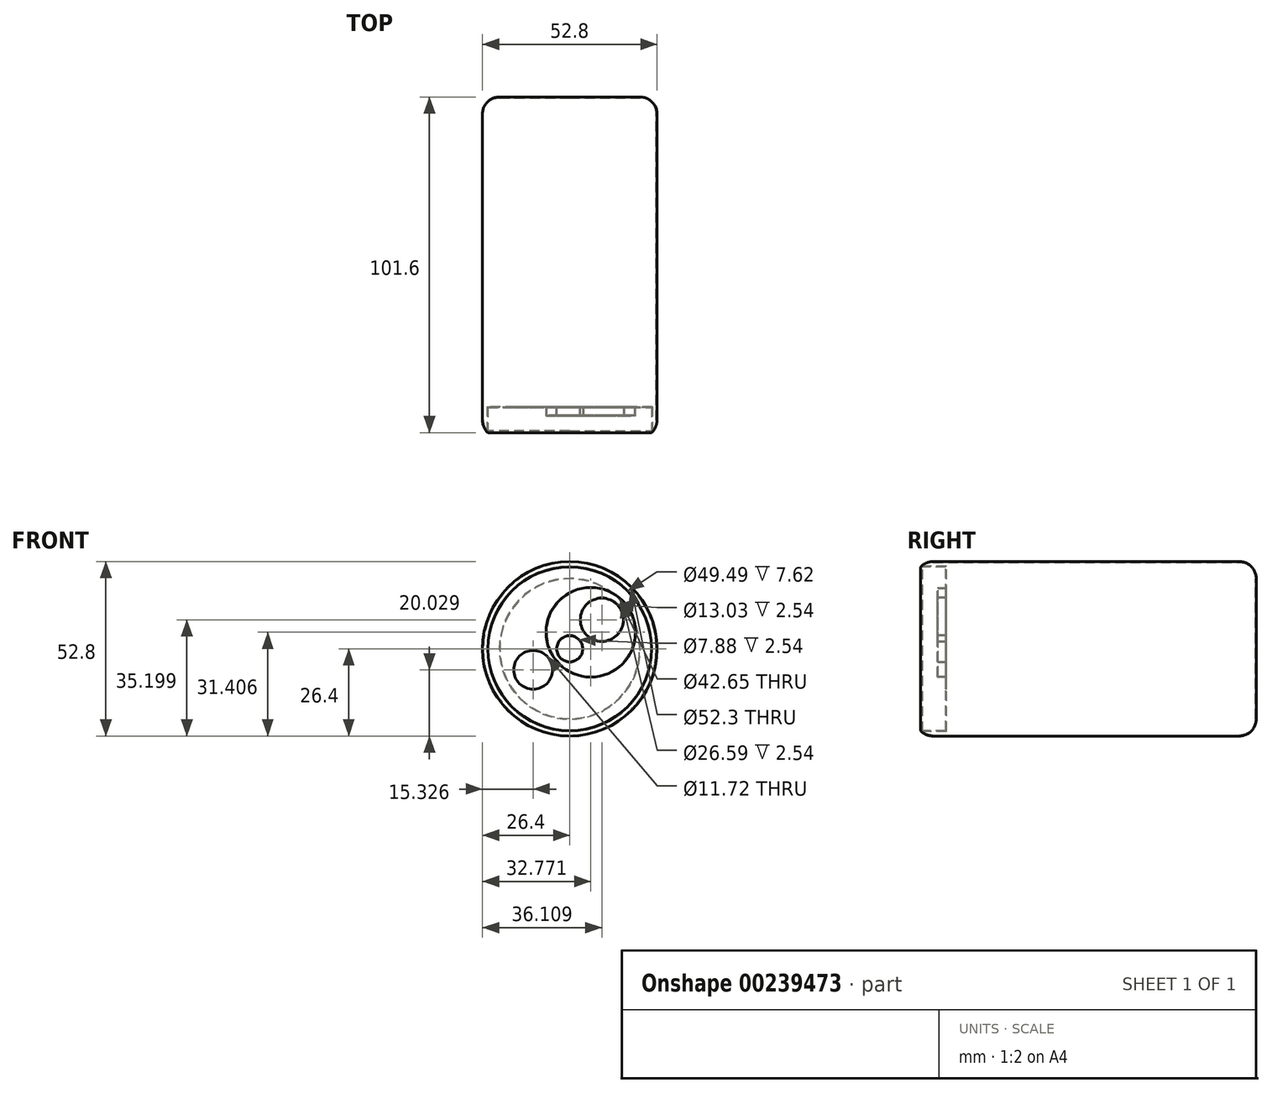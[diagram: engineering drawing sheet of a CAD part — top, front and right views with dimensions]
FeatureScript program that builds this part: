
annotation { "Feature Type Name" : "Feature", "Feature Type Description" : "" }
export const myFeature = defineFeature(function(context is Context, id is Id, definition is map)
    precondition{}
    {
        {
            var Q0;
            Q0=qCreatedBy(makeId("Front.planeOp"),FACE);
            var sketch = newSketch(context, id + "F0", { "sketchPlane" : qUnion([Q0])});
            skCircle(sketch, "E0", {"center": v(0, 0) * mm, "radius": 26.4 * mm});
            skSolve(sketch);
        }
        {
            var Q0;
            Q0=makeQuery(id+"F0.imprint","IMPRINT",FACE,{"disambiguationData":[TD([[makeQuery(id+"F0.imprint","IMPRINT",EDGE,{"derivedFrom":sQuery(id+"F0.wireOp",EDGE,"E0")}),1.0]])]});
            extrude(context, id + "F1", {"entities" : qUnion([Q0]), "depth" : 101.6 * mm});
        }
        {
            var Q0;
            Q0=makeQuery(id+"F1.opExtrude","CAP_FACE",FACE,{"disambiguationData":[OSD([sQuery(id+"F0.wireOp",EDGE,"E0")])],"isStart":false});
            var sketch = newSketch(context, id + "F2", { "sketchPlane" : qUnion([Q0])});
            skCircle(sketch, "E1", {"center": v(0, 0) * mm, "radius": 24.74 * mm});
            skSolve(sketch);
        }
        {
            var Q0;
            Q0=makeQuery(id+"F2.imprint","IMPRINT",FACE,{"disambiguationData":[TD([[makeQuery(id+"F2.imprint","IMPRINT",EDGE,{"derivedFrom":sQuery(id+"F2.wireOp",EDGE,"E1")}),1.0]])]});
            extrude(context, id + "F3", {"entities" : qUnion([Q0]), "operationType" : NewBodyOperationType.REMOVE, "oppositeDirection" : true, "depth" : 7.62 * mm});
        }
        {
            var Q0;
            Q0=makeQuery(id+"F1.opExtrude","CAP_EDGE",EDGE,{"disambiguationData":[OSD([sQuery(id+"F0.wireOp",EDGE,"E0")])],"isStart":false});
            var Q1;
            Q1=makeQuery(id+"F1.opExtrude","CAP_EDGE",EDGE,{"disambiguationData":[OSD([sQuery(id+"F0.wireOp",EDGE,"E0")])],"isStart":true});
            fillet(context, id + "F4", {"entities" : qUnion([Q0, Q1]), "radius" : 5.08 * mm, "tangentPropagation" : true, "allowEdgeOverflow" : false});
        }
        {
            var Q0;
            Q0=makeQuery(id+"F3.boolean.opBoolean","COPY",FACE,{"derivedFrom":makeQuery(id+"F3.opExtrude","CAP_FACE",FACE,{"disambiguationData":[OSD([sQuery(id+"F2.wireOp",EDGE,"E1")])],"isStart":false})});
            var sketch = newSketch(context, id + "F5", { "sketchPlane" : qUnion([Q0])});
            skCircle(sketch, "E2", {"center": v(6.37, 5) * mm, "radius": 13.55 * mm});
            skSolve(sketch);
        }
        {
            var Q0;
            Q0 = qSketchRegion(id + "F5", true);
            extrude(context, id + "F6", {"entities" : qUnion([Q0]), "operationType" : NewBodyOperationType.ADD, "depth" : 2.54 * mm});
        }
        {
            var Q0;
            Q0=makeQuery(id+"F6.opExtrude","CAP_FACE",FACE,{"disambiguationData":[OSD([sQuery(id+"F5.wireOp",EDGE,"E2")])],"isStart":false});
            var sketch = newSketch(context, id + "F7", { "sketchPlane" : qUnion([Q0])});
            skCircle(sketch, "E3", {"center": v(9.7, 8.8) * mm, "radius": 6.51 * mm});
            skSolve(sketch);
        }
        {
            var Q0;
            Q0 = qSketchRegion(id + "F7", true);
            extrude(context, id + "F8", {"entities" : qUnion([Q0]), "operationType" : NewBodyOperationType.REMOVE, "oppositeDirection" : true, "depth" : 2.54 * mm});
        }
        {
            var Q0;
            Q0=makeQuery(id+"F6.opExtrude","CAP_FACE",FACE,{"disambiguationData":[OSD([sQuery(id+"F5.wireOp",EDGE,"E2")])],"isStart":false});
            var sketch = newSketch(context, id + "F9", { "sketchPlane" : qUnion([Q0])});
            skCircle(sketch, "E4", {"center": v(0, 0) * mm, "radius": 3.94 * mm});
            skSolve(sketch);
        }
        {
            var Q0;
            Q0 = qSketchRegion(id + "F9", true);
            extrude(context, id + "F10", {"entities" : qUnion([Q0]), "operationType" : NewBodyOperationType.REMOVE, "oppositeDirection" : true, "depth" : 2.54 * mm});
        }
        {
            var Q0;
            Q0=makeQuery(id+"F1.opExtrude","CAP_FACE",FACE,{"disambiguationData":[OSD([sQuery(id+"F0.wireOp",EDGE,"E0")])],"isStart":true});
            shell(context, id + "F11", {"entities" : qUnion([Q0]), "thickness" : 0.25 * mm});
        }
        {
            var Q0;
            Q0=qCreatedBy(makeId("Front.planeOp"),FACE);
            var sketch = newSketch(context, id + "F12", { "sketchPlane" : qUnion([Q0])});
            skCircle(sketch, "E5", {"center": v(0, 0) * mm, "radius": 21.15 * mm});
            skSolve(sketch);
        }
        {
            var Q0;
            Q0=makeQuery(id+"F12.imprint","IMPRINT",FACE,{"disambiguationData":[TD([[makeQuery(id+"F12.imprint","IMPRINT",EDGE,{"derivedFrom":sQuery(id+"F12.wireOp",EDGE,"E5")}),1.0]])]});
            extrude(context, id + "F13", {"entities" : qUnion([Q0]), "depth" : 0.25 * mm});
        }
        {
            var Q0;
            Q0=makeQuery(id+"F3.boolean.opBoolean","COPY",FACE,{"derivedFrom":makeQuery(id+"F3.opExtrude","CAP_FACE",FACE,{"disambiguationData":[OSD([sQuery(id+"F2.wireOp",EDGE,"E1")])],"isStart":false})});
            var sketch = newSketch(context, id + "F14", { "sketchPlane" : qUnion([Q0])});
            skCircle(sketch, "E6", {"center": v(-11.07, -6.37) * mm, "radius": 5.86 * mm});
            skSolve(sketch);
        }
        {
            var Q0;
            Q0 = qSketchRegion(id + "F14", true);
            extrude(context, id + "F15", {"entities" : qUnion([Q0]), "operationType" : NewBodyOperationType.REMOVE, "oppositeDirection" : true, "depth" : 25.4 * mm});
        }
    });
